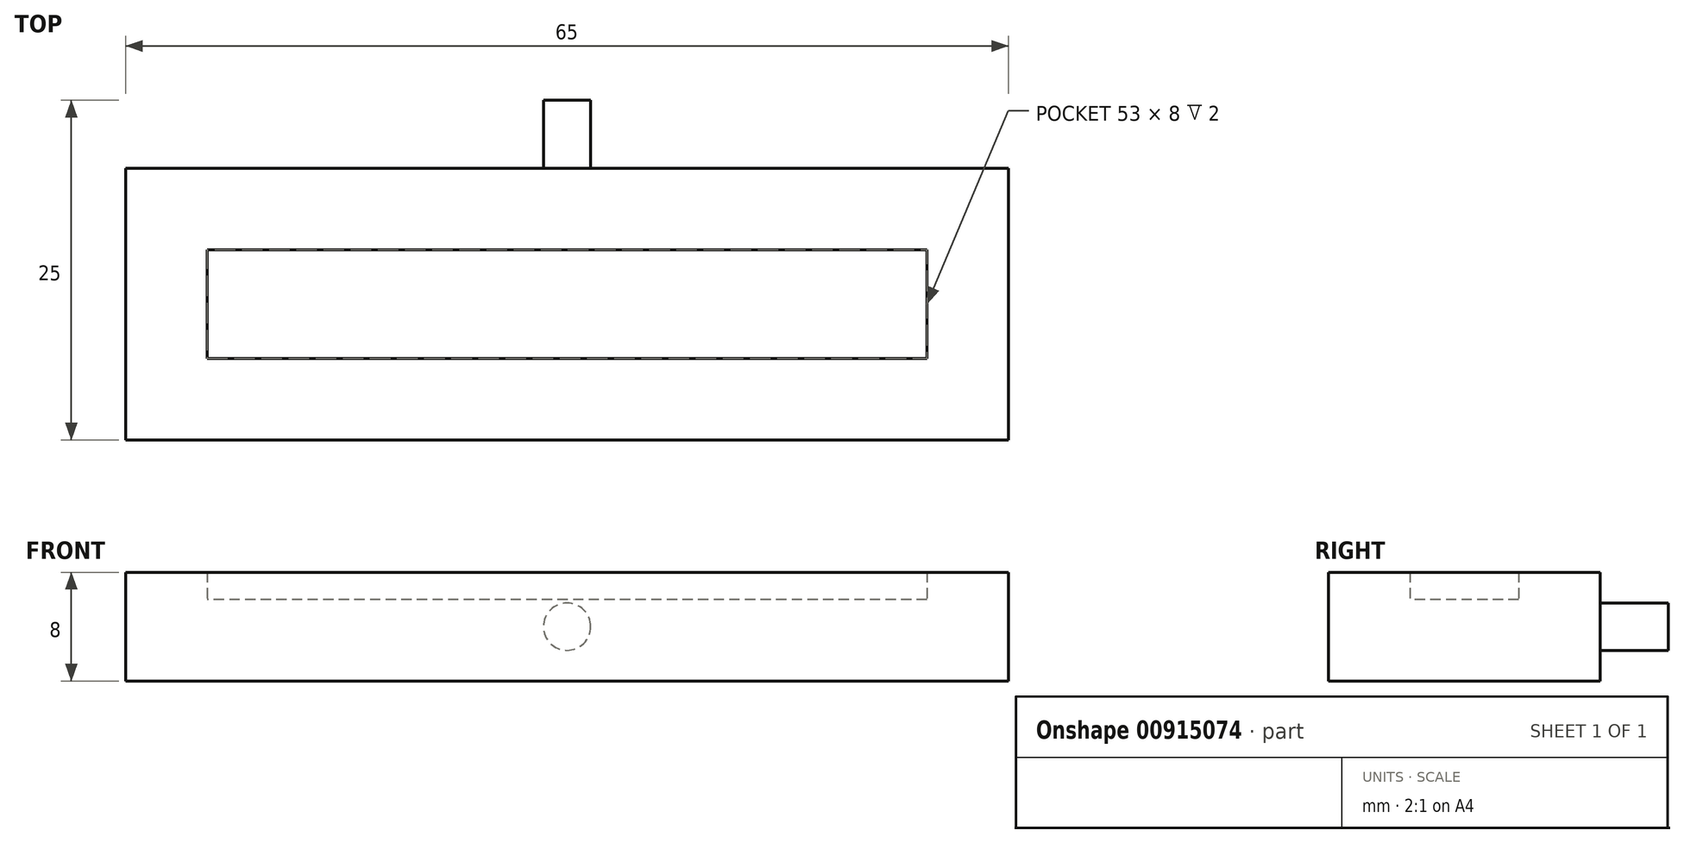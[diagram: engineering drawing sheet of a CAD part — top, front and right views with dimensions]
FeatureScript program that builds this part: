
annotation { "Feature Type Name" : "Feature", "Feature Type Description" : "" }
export const myFeature = defineFeature(function(context is Context, id is Id, definition is map)
    precondition{}
    {
        {
            var Q0;
            Q0=qCreatedBy(makeId("Top.planeOp"),FACE);
            var sketch = newSketch(context, id + "F0", { "sketchPlane" : qUnion([Q0])});
            skLineSegment(sketch, "E0.bottom", {"start": v(32.5, 10) * mm, "end": v(-32.5, 10) * mm});
            skLineSegment(sketch, "E0.top", {"start": v(32.5, -10) * mm, "end": v(-32.5, -10) * mm});
            skLineSegment(sketch, "E0.left", {"start": v(32.5, 10) * mm, "end": v(32.5, -10) * mm});
            skLineSegment(sketch, "E0.right", {"start": v(-32.5, 10) * mm, "end": v(-32.5, -10) * mm});
            skPoint(sketch, "E0.middle", {"position": v(0, 0) * mm});
            skSolve(sketch);
        }
        {
            var Q0;
            Q0=makeQuery(id+"F0.imprint","IMPRINT",FACE,{"disambiguationData":[TD([[makeQuery(id+"F0.imprint","IMPRINT",EDGE,{"derivedFrom":sQuery(id+"F0.wireOp",EDGE,"E0.bottom")}),1.0]])]});
            extrude(context, id + "F1", {"entities" : qUnion([Q0]), "depth" : 8 * mm, "offsetDistance" : 25 * mm});
        }
        {
            var Q0;
            Q0=makeQuery(id+"F1.opExtrude","CAP_FACE",FACE,{"disambiguationData":[OSD([sQuery(id+"F0.wireOp",EDGE,"E0.bottom"),sQuery(id+"F0.wireOp",EDGE,"E0.top"),sQuery(id+"F0.wireOp",EDGE,"E0.left"),sQuery(id+"F0.wireOp",EDGE,"E0.right")])],"isStart":false});
            shell(context, id + "F2", {"entities" : qUnion([Q0]), "thickness" : 6 * mm});
        }
        {
            var Q0;
            Q0=makeQuery(id+"F1.opExtrude","SWEPT_FACE",FACE,{"disambiguationData":[OSD([sQuery(id+"F0.wireOp",EDGE,"E0.bottom")])]});
            var sketch = newSketch(context, id + "F3", { "sketchPlane" : qUnion([Q0])});
            skLineSegment(sketch, "E1", {"start": v(0, 8) * mm, "end": v(0, 4) * mm});
            skLineSegment(sketch, "E2", {"start": v(0, 4) * mm, "end": v(0, 0) * mm});
            skCircle(sketch, "E3", {"center": v(0, 4) * mm, "radius": 1.74 * mm});
            skSolve(sketch);
        }
        {
            var Q0;
            {var subQ0=sQuery(id+"F3.wireOp",EDGE,"E2");var subQ1=sQuery(id+"F3.wireOp",EDGE,"E1");var subQ2=makeQuery(id+"F3.imprint","INTERSECT",VERTEX,{"derivedFrom":[subQ1,subQ0]});Q0=makeQuery(id+"F3.imprint","IMPRINT",FACE,{"disambiguationData":[TD([[makeQuery(id+"F3.imprint","IMPRINT",EDGE,{"disambiguationData":[TD([[subQ2,1.0]])],"derivedFrom":subQ1}),1.0]])]});}
            var Q1;
            {var subQ0=sQuery(id+"F3.wireOp",EDGE,"E2");var subQ1=sQuery(id+"F3.wireOp",EDGE,"E1");var subQ2=makeQuery(id+"F3.imprint","INTERSECT",VERTEX,{"derivedFrom":[subQ1,subQ0]});Q1=makeQuery(id+"F3.imprint","IMPRINT",FACE,{"disambiguationData":[TD([[makeQuery(id+"F3.imprint","IMPRINT",EDGE,{"disambiguationData":[TD([[subQ2,1.0]])],"derivedFrom":subQ1}),-1.0]])]});}
            extrude(context, id + "F4", {"entities" : qUnion([Q0, Q1]), "operationType" : NewBodyOperationType.ADD, "depth" : 5 * mm, "offsetDistance" : 25 * mm});
        }
    });
